# Revit family: okamura_ML1EHE_ライブス シェルフ_コートハンガーユニット_木棚板_900W×450D×2236H
name_source: partatom
category: 家具
revit_build: Autodesk Revit 2017 (Build: 20160225_1515(x64)
units: mm (PartAtom-declared; Revit-internal decimal feet)

## family parameters
OmniClass タイトル = General Furniture and Specialties
OmniClass 番号 = 23.40.20.00
ロード時にボイドで切り取り = いいえ
作業面に基づく = いいえ
共有 = いいえ
常に垂直 = はい
部屋計算ポイント = いいえ

## types (14) — shared parameters
D = 450  [stored 1.47638 ft]
H = 2236  [stored 7.33596 ft]
URL = http://www.okamura.co.jp
W = 900  [stored 2.95276 ft]
アセンブリ コード = E2020200
キーノート = 12490
区分 = シェルフ
製品カテゴリ = クリエイティブファニチュア
製品コード/色仕様 = ML1EHE
製造元 = 株式会社オカムラ

## per-type parameters (varying)
| type | 天板 | 支柱 |
| MDY7（プライズウッドライト/ブラック） | okm_MX61 | okm_Z25 |
| MDY8（プライズウッドミディアム/ブラック） | okm_MX62 | okm_Z25 |
| MDY9（プライズウッドダーク/ブラック） | okm_MX63 | okm_Z25 |
| MU03（プライズウッドライト/ネオホワイト） | okm_MX61 | okm_ZA75 |
| MU04（プライズウッドミディアム/ネオホワイト） | okm_MX62 | okm_ZA75 |
| MU05（プライズウッドダーク/ネオホワイト） | okm_MX63 | okm_ZA75 |
| MGM4（ビンテージエルム/ネオホワイト） | okm_MEP4 | okm_ZA75 |
| MGM1（チョークドエルム/ネオホワイト） | okm_MEP1 | okm_ZA75 |
| MGM2（ソーンオーク/ネオホワイト） | okm_MEP2 | okm_ZA75 |
| MGM3（ラスティックパイン/ネオホワイト） | okm_MEP3 | okm_ZA75 |
| MGL4（ビンテージエルム/ブラック） | okm_MEP4 | okm_Z25 |
| MGL1（チョークドエルム/ブラック） | okm_MEP1 | okm_Z25 |
| MGL2（ソーンオーク/ブラック） | okm_MEP2 | okm_Z25 |
| MGL3（ラスティックパイン/ブラック） | okm_MEP3 | okm_Z25 |

note: [stored X ft] marks values corroborated as IEEE doubles in the binary element streams (Revit-internal decimal feet)
